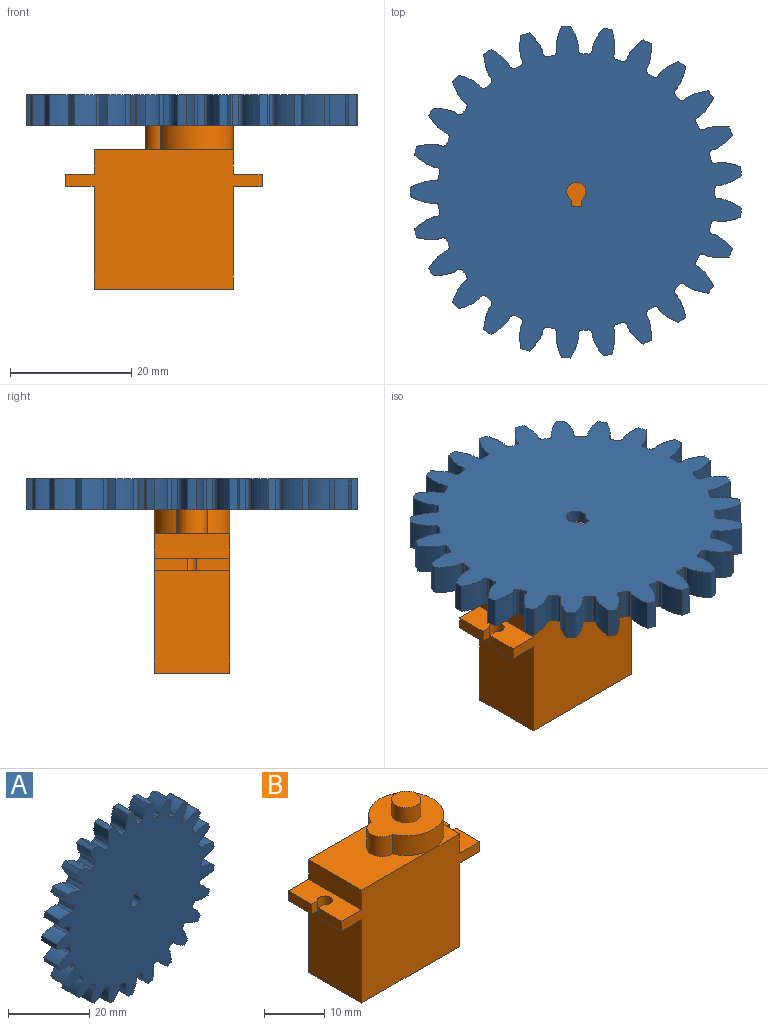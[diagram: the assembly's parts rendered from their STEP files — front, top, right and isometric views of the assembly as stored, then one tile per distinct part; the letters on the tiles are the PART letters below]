
ASSEMBLY  parts=2 mates=1
PART A: 156 faces, bbox 54.7x5.1x54.8 mm
  f0: cylinder r=27.43mm len=5.08mm, axis (0,1,0), area 7.4mm2, adj f24,f30,f141,f153
  f1: cylinder r=27.43mm len=5.08mm, axis (0,1,0), area 7.4mm2, adj f24,f30,f148,f151
  f2: cylinder r=27.43mm len=5.08mm, axis (0,1,0), area 7.4mm2, adj f24,f30,f136,f143
  f3: cylinder r=27.43mm len=5.08mm, axis (0,1,0), area 7.4mm2, adj f24,f30,f131,f138
  f4: cylinder r=27.43mm len=5.08mm, axis (0,1,0), area 7.4mm2, adj f24,f30,f126,f133
  f5: cylinder r=27.43mm len=5.08mm, axis (0,1,0), area 7.4mm2, adj f24,f30,f116,f128
  f6: cylinder r=27.43mm len=5.08mm, axis (0,1,0), area 7.4mm2, adj f24,f30,f111,f123
  f7: cylinder r=27.43mm len=5.08mm, axis (0,1,0), area 7.4mm2, adj f24,f30,f118,f121
  f8: cylinder r=27.43mm len=5.08mm, axis (0,1,0), area 7.4mm2, adj f24,f30,f106,f113
  f9: cylinder r=27.43mm len=5.08mm, axis (0,1,0), area 7.4mm2, adj f24,f30,f101,f108
  f10: cylinder r=27.43mm len=5.08mm, axis (0,1,0), area 7.4mm2, adj f24,f30,f96,f103
  f11: cylinder r=27.43mm len=5.08mm, axis (0,1,0), area 7.4mm2, adj f24,f30,f81,f98
  f12: cylinder r=27.43mm len=5.08mm, axis (0,1,0), area 7.4mm2, adj f24,f30,f31,f93
  f13: cylinder r=27.43mm len=5.08mm, axis (0,1,0), area 7.4mm2, adj f24,f30,f88,f91
  f14: cylinder r=27.43mm len=5.08mm, axis (0,1,0), area 7.4mm2, adj f24,f30,f76,f83
  f15: cylinder r=27.43mm len=5.08mm, axis (0,1,0), area 7.4mm2, adj f24,f30,f78,f86
  f16: cylinder r=27.43mm len=5.08mm, axis (0,1,0), area 7.4mm2, adj f24,f30,f73,f146
  f17: cylinder r=27.43mm len=5.08mm, axis (0,1,0), area 7.4mm2, adj f24,f30,f68,f71
  f18: cylinder r=27.43mm len=5.08mm, axis (0,1,0), area 7.4mm2, adj f24,f30,f63,f66
  f19: cylinder r=27.43mm len=5.08mm, axis (0,1,0), area 7.4mm2, adj f24,f30,f58,f61
  f20: cylinder r=27.43mm len=5.08mm, axis (0,1,0), area 7.4mm2, adj f24,f30,f46,f53
  f21: cylinder r=27.43mm len=5.08mm, axis (0,1,0), area 7.4mm2, adj f24,f30,f36,f48
  f22: cylinder r=27.43mm len=5.08mm, axis (0,1,0), area 7.4mm2, adj f24,f30,f43,f56
  f23: cylinder r=27.43mm len=5.08mm, axis (0,1,0), area 7.4mm2, adj f24,f30,f38,f41
  f24: plane 54.85x54.74mm, normal (0,-1,0), area 1985mm2, adj f0,f1,f2,f3,f4,f5,f6,f7
  f25: plane 5.08x1.01mm, normal (-1,0,0), area 5.1mm2, adj f24,f26,f28,f30
  f26: cylinder r=1.59mm len=5.08mm, axis (0,1,0), area 42.2mm2, adj f24,f25,f27,f30
  f27: plane 5.08x1.01mm, normal (1,0,0), area 5.1mm2, adj f24,f26,f28,f30
  f28: plane 5.08x1.59mm, normal (0,0,-1), area 8.1mm2, adj f24,f25,f27,f30
  f29: cylinder r=27.43mm len=5.08mm, axis (0,1,0), area 7.4mm2, adj f24,f30,f33,f51
  f30: plane 54.85x54.74mm, normal (0,1,0), area 1985mm2, adj f0,f1,f2,f3,f4,f5,f6,f7
  f31: extruded ~5.08x3.89mm, area 21.7mm2, adj f12,f24,f30,f34
  f32: cylinder r=22.86mm len=5.08mm, axis (0,1,0), area 5.4mm2, adj f24,f30,f34,f35
  f33: extruded ~5.08x3.89mm, area 21.7mm2, adj f24,f29,f30,f35
  f34: cylinder r=0.58mm len=5.08mm, axis (0,1,0), area 4.5mm2, adj f24,f30,f31,f32
  f35: cylinder r=0.58mm len=5.08mm, axis (0,1,0), area 4.5mm2, adj f24,f30,f32,f33
  f36: extruded ~5.08x3.93mm, area 21.7mm2, adj f21,f24,f30,f39
  f37: cylinder r=22.86mm len=5.08mm, axis (0,1,0), area 5.4mm2, adj f24,f30,f39,f40
  f38: extruded ~5.08x3.83mm, area 21.7mm2, adj f23,f24,f30,f40
  f39: cylinder r=0.58mm len=5.08mm, axis (0,1,0), area 4.5mm2, adj f24,f30,f36,f37
  f40: cylinder r=0.58mm len=5.08mm, axis (0,1,0), area 4.5mm2, adj f24,f30,f37,f38
  f41: extruded ~5.08x3.43mm, area 21.7mm2, adj f23,f24,f30,f44
  f42: cylinder r=22.86mm len=5.08mm, axis (0,1,0), area 5.4mm2, adj f24,f30,f44,f45
  f43: extruded ~5.08x4.14mm, area 21.7mm2, adj f22,f24,f30,f45
  f44: cylinder r=0.58mm len=5.08mm, axis (0,1,0), area 4.5mm2, adj f24,f30,f41,f42
  f45: cylinder r=0.58mm len=5.08mm, axis (0,1,0), area 4.5mm2, adj f24,f30,f42,f43
  f46: extruded ~5.08x4.18mm, area 21.7mm2, adj f20,f24,f30,f49
  f47: cylinder r=22.86mm len=5.08mm, axis (0,1,0), area 5.4mm2, adj f24,f30,f49,f50
  f48: extruded ~5.08x3.27mm, area 21.7mm2, adj f21,f24,f30,f50
  f49: cylinder r=0.58mm len=5.08mm, axis (0,1,0), area 4.5mm2, adj f24,f30,f46,f47
  f50: cylinder r=0.58mm len=5.08mm, axis (0,1,0), area 4.5mm2, adj f24,f30,f47,f48
  f51: extruded ~5.08x4.17mm, area 21.7mm2, adj f24,f29,f30,f54
  f52: cylinder r=22.86mm len=5.08mm, axis (0,1,0), area 5.4mm2, adj f24,f30,f54,f55
  f53: extruded ~5.08x3.38mm, area 21.7mm2, adj f20,f24,f30,f55
  f54: cylinder r=0.58mm len=5.08mm, axis (0,1,0), area 4.5mm2, adj f24,f30,f51,f52
  f55: cylinder r=0.58mm len=5.08mm, axis (0,1,0), area 4.5mm2, adj f24,f30,f52,f53
  f56: extruded ~5.08x3.21mm, area 21.7mm2, adj f22,f24,f30,f59
  f57: cylinder r=22.86mm len=5.08mm, axis (0,1,0), area 5.4mm2, adj f24,f30,f59,f60
  f58: extruded ~5.08x4.2mm, area 21.7mm2, adj f19,f24,f30,f60
  f59: cylinder r=0.58mm len=5.08mm, axis (0,1,0), area 4.5mm2, adj f24,f30,f56,f57
  f60: cylinder r=0.58mm len=5.08mm, axis (0,1,0), area 4.5mm2, adj f24,f30,f57,f58
  f61: extruded ~5.08x3.79mm, area 21.7mm2, adj f19,f24,f30,f64
  f62: cylinder r=22.86mm len=5.08mm, axis (0,1,0), area 5.4mm2, adj f24,f30,f64,f65
  f63: extruded ~5.08x3.99mm, area 21.7mm2, adj f18,f24,f30,f65
  f64: cylinder r=0.58mm len=5.08mm, axis (0,1,0), area 4.5mm2, adj f24,f30,f61,f62
  f65: cylinder r=0.58mm len=5.08mm, axis (0,1,0), area 4.5mm2, adj f24,f30,f62,f63
  f66: extruded ~5.08x4.12mm, area 21.7mm2, adj f18,f24,f30,f69
  f67: cylinder r=22.86mm len=5.08mm, axis (0,1,0), area 5.4mm2, adj f24,f30,f69,f70
  f68: extruded ~5.08x3.53mm, area 21.7mm2, adj f17,f24,f30,f70
  f69: cylinder r=0.58mm len=5.08mm, axis (0,1,0), area 4.5mm2, adj f24,f30,f66,f67
  f70: cylinder r=0.58mm len=5.08mm, axis (0,1,0), area 4.5mm2, adj f24,f30,f67,f68
  f71: extruded ~5.08x4.2mm, area 21.7mm2, adj f17,f24,f30,f74
  f72: cylinder r=22.86mm len=5.08mm, axis (0,1,0), area 5.4mm2, adj f24,f30,f74,f75
  f73: extruded ~5.08x3.1mm, area 21.7mm2, adj f16,f24,f30,f75
  f74: cylinder r=0.58mm len=5.08mm, axis (0,1,0), area 4.5mm2, adj f24,f30,f71,f72
  f75: cylinder r=0.58mm len=5.08mm, axis (0,1,0), area 4.5mm2, adj f24,f30,f72,f73
  f76: extruded ~5.08x3.83mm, area 21.7mm2, adj f14,f24,f30,f79
  f77: cylinder r=22.86mm len=5.08mm, axis (0,1,0), area 5.4mm2, adj f24,f30,f79,f80
  f78: extruded ~5.08x3.93mm, area 21.7mm2, adj f15,f24,f30,f80
  f79: cylinder r=0.58mm len=5.08mm, axis (0,1,0), area 4.5mm2, adj f24,f30,f76,f77
  f80: cylinder r=0.58mm len=5.08mm, axis (0,1,0), area 4.5mm2, adj f24,f30,f77,f78
  f81: extruded ~5.08x4.14mm, area 21.7mm2, adj f11,f24,f30,f84
  f82: cylinder r=22.86mm len=5.08mm, axis (0,1,0), area 5.4mm2, adj f24,f30,f84,f85
  f83: extruded ~5.08x3.43mm, area 21.7mm2, adj f14,f24,f30,f85
  f84: cylinder r=0.58mm len=5.08mm, axis (0,1,0), area 4.5mm2, adj f24,f30,f81,f82
  f85: cylinder r=0.58mm len=5.08mm, axis (0,1,0), area 4.5mm2, adj f24,f30,f82,f83
  f86: extruded ~5.08x3.27mm, area 21.7mm2, adj f15,f24,f30,f89
  f87: cylinder r=22.86mm len=5.08mm, axis (0,1,0), area 5.4mm2, adj f24,f30,f89,f90
  f88: extruded ~5.08x4.18mm, area 21.7mm2, adj f13,f24,f30,f90
  f89: cylinder r=0.58mm len=5.08mm, axis (0,1,0), area 4.5mm2, adj f24,f30,f86,f87
  f90: cylinder r=0.58mm len=5.08mm, axis (0,1,0), area 4.5mm2, adj f24,f30,f87,f88
  f91: extruded ~5.08x3.38mm, area 21.7mm2, adj f13,f24,f30,f94
  f92: cylinder r=22.86mm len=5.08mm, axis (0,1,0), area 5.4mm2, adj f24,f30,f94,f95
  f93: extruded ~5.08x4.17mm, area 21.7mm2, adj f12,f24,f30,f95
  f94: cylinder r=0.58mm len=5.08mm, axis (0,1,0), area 4.5mm2, adj f24,f30,f91,f92
  f95: cylinder r=0.58mm len=5.08mm, axis (0,1,0), area 4.5mm2, adj f24,f30,f92,f93
  f96: extruded ~5.08x4.2mm, area 21.7mm2, adj f10,f24,f30,f99
  f97: cylinder r=22.86mm len=5.08mm, axis (0,1,0), area 5.4mm2, adj f24,f30,f99,f100
  f98: extruded ~5.08x3.21mm, area 21.7mm2, adj f11,f24,f30,f100
  f99: cylinder r=0.58mm len=5.08mm, axis (0,1,0), area 4.5mm2, adj f24,f30,f96,f97
  f100: cylinder r=0.58mm len=5.08mm, axis (0,1,0), area 4.5mm2, adj f24,f30,f97,f98
  f101: extruded ~5.08x3.99mm, area 21.7mm2, adj f9,f24,f30,f104
  f102: cylinder r=22.86mm len=5.08mm, axis (0,1,0), area 5.4mm2, adj f24,f30,f104,f105
  f103: extruded ~5.08x3.79mm, area 21.7mm2, adj f10,f24,f30,f105
  f104: cylinder r=0.58mm len=5.08mm, axis (0,1,0), area 4.5mm2, adj f24,f30,f101,f102
  f105: cylinder r=0.58mm len=5.08mm, axis (0,1,0), area 4.5mm2, adj f24,f30,f102,f103
  f106: extruded ~5.08x3.53mm, area 21.7mm2, adj f8,f24,f30,f109
  f107: cylinder r=22.86mm len=5.08mm, axis (0,1,0), area 5.4mm2, adj f24,f30,f109,f110
  f108: extruded ~5.08x4.12mm, area 21.7mm2, adj f9,f24,f30,f110
  f109: cylinder r=0.58mm len=5.08mm, axis (0,1,0), area 4.5mm2, adj f24,f30,f106,f107
  f110: cylinder r=0.58mm len=5.08mm, axis (0,1,0), area 4.5mm2, adj f24,f30,f107,f108
  f111: extruded ~5.08x3.1mm, area 21.7mm2, adj f6,f24,f30,f114
  f112: cylinder r=22.86mm len=5.08mm, axis (0,1,0), area 5.4mm2, adj f24,f30,f114,f115
  f113: extruded ~5.08x4.2mm, area 21.7mm2, adj f8,f24,f30,f115
  f114: cylinder r=0.58mm len=5.08mm, axis (0,1,0), area 4.5mm2, adj f24,f30,f111,f112
  f115: cylinder r=0.58mm len=5.08mm, axis (0,1,0), area 4.5mm2, adj f24,f30,f112,f113
  f116: extruded ~5.08x4.09mm, area 21.7mm2, adj f5,f24,f30,f119
  f117: cylinder r=22.86mm len=5.08mm, axis (0,1,0), area 5.4mm2, adj f24,f30,f119,f120
  f118: extruded ~5.08x3.58mm, area 21.7mm2, adj f7,f24,f30,f120
  f119: cylinder r=0.58mm len=5.08mm, axis (0,1,0), area 4.5mm2, adj f24,f30,f116,f117
  f120: cylinder r=0.58mm len=5.08mm, axis (0,1,0), area 4.5mm2, adj f24,f30,f117,f118
  f121: extruded ~5.08x3.71mm, area 21.7mm2, adj f7,f24,f30,f124
  f122: cylinder r=22.86mm len=5.08mm, axis (0,1,0), area 5.4mm2, adj f24,f30,f124,f125
  f123: extruded ~5.08x4.02mm, area 21.7mm2, adj f6,f24,f30,f125
  f124: cylinder r=0.58mm len=5.08mm, axis (0,1,0), area 4.5mm2, adj f24,f30,f121,f122
  f125: cylinder r=0.58mm len=5.08mm, axis (0,1,0), area 4.5mm2, adj f24,f30,f122,f123
  f126: extruded ~5.08x4.21mm, area 21.7mm2, adj f4,f24,f30,f129
  f127: cylinder r=22.86mm len=5.08mm, axis (0,1,0), area 5.4mm2, adj f24,f30,f129,f130
  f128: extruded ~5.08x3.03mm, area 21.7mm2, adj f5,f24,f30,f130
  f129: cylinder r=0.58mm len=5.08mm, axis (0,1,0), area 4.5mm2, adj f24,f30,f126,f127
  f130: cylinder r=0.58mm len=5.08mm, axis (0,1,0), area 4.5mm2, adj f24,f30,f127,f128
  f131: extruded ~5.08x4.06mm, area 21.7mm2, adj f3,f24,f30,f134
  f132: cylinder r=22.86mm len=5.08mm, axis (0,1,0), area 5.4mm2, adj f24,f30,f134,f135
  f133: extruded ~5.08x3.66mm, area 21.7mm2, adj f4,f24,f30,f135
  f134: cylinder r=0.58mm len=5.08mm, axis (0,1,0), area 4.5mm2, adj f24,f30,f131,f132
  f135: cylinder r=0.58mm len=5.08mm, axis (0,1,0), area 4.5mm2, adj f24,f30,f132,f133
  f136: extruded ~5.08x3.66mm, area 21.7mm2, adj f2,f24,f30,f139
  f137: cylinder r=22.86mm len=5.08mm, axis (0,1,0), area 5.4mm2, adj f24,f30,f139,f140
  f138: extruded ~5.08x4.06mm, area 21.7mm2, adj f3,f24,f30,f140
  f139: cylinder r=0.58mm len=5.08mm, axis (0,1,0), area 4.5mm2, adj f24,f30,f136,f137
  f140: cylinder r=0.58mm len=5.08mm, axis (0,1,0), area 4.5mm2, adj f24,f30,f137,f138
  f141: extruded ~5.08x3.03mm, area 21.7mm2, adj f0,f24,f30,f144
  f142: cylinder r=22.86mm len=5.08mm, axis (0,1,0), area 5.4mm2, adj f24,f30,f144,f145
  f143: extruded ~5.08x4.21mm, area 21.7mm2, adj f2,f24,f30,f145
  f144: cylinder r=0.58mm len=5.08mm, axis (0,1,0), area 4.5mm2, adj f24,f30,f141,f142
  f145: cylinder r=0.58mm len=5.08mm, axis (0,1,0), area 4.5mm2, adj f24,f30,f142,f143
  f146: extruded ~5.08x4.02mm, area 21.7mm2, adj f16,f24,f30,f149
  f147: cylinder r=22.86mm len=5.08mm, axis (0,1,0), area 5.4mm2, adj f24,f30,f149,f150
  f148: extruded ~5.08x3.71mm, area 21.7mm2, adj f1,f24,f30,f150
  f149: cylinder r=0.58mm len=5.08mm, axis (0,1,0), area 4.5mm2, adj f24,f30,f146,f147
  f150: cylinder r=0.58mm len=5.08mm, axis (0,1,0), area 4.5mm2, adj f24,f30,f147,f148
  f151: extruded ~5.08x3.58mm, area 21.7mm2, adj f1,f24,f30,f154
  f152: cylinder r=22.86mm len=5.08mm, axis (0,1,0), area 5.4mm2, adj f24,f30,f154,f155
  f153: extruded ~5.08x4.09mm, area 21.7mm2, adj f0,f24,f30,f155
  f154: cylinder r=0.58mm len=5.08mm, axis (0,1,0), area 4.5mm2, adj f24,f30,f151,f152
  f155: cylinder r=0.58mm len=5.08mm, axis (0,1,0), area 4.5mm2, adj f24,f30,f152,f153
PART B: 29 faces, bbox 32.5x12.6x30 mm
  f0: plane 4.99x4.9mm, normal (0,0,1), area 18.9mm2, adj f1
  f1: cylinder r=2.45mm len=4.9mm, axis (0,0,1), area 46.2mm2, adj f0,f2
  f2: plane 14.61x12.65mm, normal (0,0,1), area 112mm2, adj f1,f3,f4
  f3: cylinder r=2.5mm len=5mm, axis (0,0,1), area 31.6mm2, adj f2,f4,f10
  f4: cylinder r=6.25mm len=12.5mm, axis (0,0,1), area 136.5mm2, adj f2,f3,f8,f10,f11
  f5: plane 2x1.38mm, normal (0,-1,0), area 2.7mm2, adj f6,f9,f13,f15
  f6: cylinder r=1.25mm len=2.5mm, axis (0,0,-1), area 12.5mm2, adj f5,f7,f13,f15
  f7: plane 2x1.38mm, normal (0,1,0), area 2.7mm2, adj f6,f13,f14,f15
  f8: plane 6.25x6.25mm, normal (0,0,1), area 8.4mm2, adj f4,f12,f20
  f9: plane 5.5x2mm, normal (1,0,0), area 11mm2, adj f5,f13,f15,f20
  f10: plane 16.75x12.5mm, normal (0,0,1), area 139.8mm2, adj f3,f4,f18,f20,f22
  f11: plane 6.25x6.25mm, normal (0,0,1), area 8.4mm2, adj f4,f12,f22
  f12: plane 12.5x4mm, normal (1,0,0), area 50mm2, adj f8,f11,f13,f20,f22
  f13: plane 12.5x4.75mm, normal (0,0,1), area 52.7mm2, adj f5,f6,f7,f9,f12,f14,f20,f22
  f14: plane 5.5x2mm, normal (1,0,0), area 11mm2, adj f7,f13,f15,f22
  f15: plane 12.5x4.75mm, normal (0,0,-1), area 52.7mm2, adj f5,f6,f7,f9,f14,f16,f20,f22
  f16: plane 17x12.5mm, normal (1,0,0), area 212.5mm2, adj f15,f17,f20,f22
  f17: plane 23x12.5mm, normal (0,0,-1), area 287.5mm2, adj f16,f20,f21,f22
  f18: plane 12.5x4mm, normal (-1,0,0), area 50mm2, adj f10,f20,f22,f25
  f19: plane 5.5x2mm, normal (-1,0,0), area 11mm2, adj f20,f24,f25,f27
  f20: plane 32.5x23mm, normal (0,1,0), area 548mm2, adj f8,f9,f10,f12,f13,f15,f16,f17
  f21: plane 17x12.5mm, normal (-1,0,0), area 212.5mm2, adj f17,f20,f22,f27
  f22: plane 32.5x23mm, normal (0,-1,0), area 548mm2, adj f10,f11,f12,f13,f14,f15,f16,f17
  f23: plane 5.5x2mm, normal (-1,0,0), area 11mm2, adj f22,f25,f26,f27
  f24: plane 2x1.38mm, normal (0,-1,0), area 2.8mm2, adj f19,f25,f27,f28
  f25: plane 12.5x4.75mm, normal (0,0,1), area 52.7mm2, adj f18,f19,f20,f22,f23,f24,f26,f28
  f26: plane 2x1.38mm, normal (0,1,0), area 2.8mm2, adj f23,f25,f27,f28
  f27: plane 12.5x4.75mm, normal (0,0,-1), area 52.7mm2, adj f19,f20,f21,f22,f23,f24,f26,f28
  f28: cylinder r=1.25mm len=2.5mm, axis (0,0,-1), area 12.5mm2, adj f24,f25,f26,f27
PLACE A rot(axis=(1,0,0),90deg) t=(-3.1,9.56,41.43)mm
PLACE B t=(3.66,3.31,9.35)mm
MATE fastened A.f0 <-> B.f2  axis (0,0,-1) through (-3.1,9.56,36.35)mm
